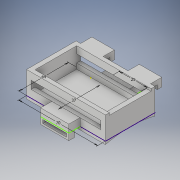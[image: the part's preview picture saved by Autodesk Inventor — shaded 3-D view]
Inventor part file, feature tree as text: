
AUTODESK INVENTOR PART (.ipt)
format: ipt  version: 2019 (Build 230136000, 136)  size: 488,448 bytes
history: native  units: mm
features: extrude x24, sketch x18
ambient origin geometry x8: Origin, YZ Plane, XZ Plane, XY Plane, X Axis, Y Axis, Z Axis, Center Point
bodies: Body1 (feature_tree)
feature tree (42):
  sketch  "Sketch1"  dims[d2=70.0mm d3=44.0mm]
  extrude  "Extrusion2"  Depth=44.0mm
  extrude  "Extrusion3"  Depth=2.0mm TaperAngle=0.0deg
  extrude  "Extrusion4"  Depth=25.0mm
  extrude  "Extrusion5"  Depth=2.0mm TaperAngle=0.0deg
  extrude  "Extrusion6"  Depth=20.0mm
  extrude  "Extrusion9"  Depth=20.0mm
  extrude  "Extrusion10"  Depth=5.0mm TaperAngle=0.0deg
  extrude  "Extrusion11"  Depth=10.0mm TaperAngle=0.0deg
  extrude  "Extrusion12"  Depth=90.0mm
  extrude  "Extrusion13"  Depth=2.0mm
  sketch  "Sketch6"  dims[d30=5.0mm d31=0.0mm d32=20.0mm]
  sketch  "Sketch7"  dims[d34=2.5mm d35=5.0mm d36=0.0mm]
  sketch  "Sketch8"  dims[d37=10.0mm d38=0.0mm d39=10.0mm d40=0.0mm]
  sketch  "Sketch9"  dims[d42=90.0mm d43=180.0mm]
  extrude  "Extrusion18"  Depth=2.0mm TaperAngle=0.0deg
  sketch  "Sketch21"  dims[d47=2.0mm d65=2.0mm d66=0.0mm]
  sketch  "Sketch25"  dims[d84=7.5mm d91=20.0mm]
  extrude  "Extrusion29"  Depth=20.0mm
  extrude  "Extrusion30"  Depth=20.0mm
  extrude  "Extrusion31"  Depth=6.0mm TaperAngle=0.0deg
  extrude  "Extrusion32"  Depth=21.0mm
  sketch  "Sketch30"  dims[d109=6.0mm d110=0.0mm d111=21.0mm]
  extrude  "Extrusion33"  Depth=6.0mm TaperAngle=0.0deg
  extrude  "Extrusion34"  Depth=6.0mm TaperAngle=0.0deg
  extrude  "Extrusion35"  Depth=6.75mm TaperAngle=0.0deg
  extrude  "Extrusion36"  Depth=6.75mm TaperAngle=0.0deg
  extrude  "Extrusion37"  Depth=6.75mm TaperAngle=0.0deg
  extrude  "Extrusion38"  Depth=6.75mm TaperAngle=0.0deg
  extrude  "Extrusion39"  Depth=10.0mm TaperAngle=0.0deg
  extrude  "Extrusion40"  Depth=10.0mm TaperAngle=0.0deg
  extrude  "Extrusion41"  Depth=20.0mm TaperAngle=0.0deg
  sketch  "Sketch34"  dims[d118=6.75mm d119=0.0mm d120=6.75mm d121=0.0mm d122=6.75mm d123=0.0mm d124=6.75mm d125=0.0mm d126=6.75mm d127=0.0mm d128=10.0mm d129=0.0mm d130=10.0mm d131=0.0mm d133=20.0mm d134=0.0mm d135=20.0mm d136=0.0mm d139=1.0mm d140=1.0mm d141=1.0mm d142=0.15mm d143=0.25mm d144=0.375mm d145=14.3117mm d146=0.75mm d147=20.594885mm d148=0.0625mm d149=0.75mm d150=0.375mm]
  sketch  "Sketch2"  dims[d6=20.0mm d7=0.0mm d8=2.0mm d9=0.0mm]
  sketch  "Sketch3"  dims[d10=45.0mm d11=0.0mm d16=25.0mm]
  sketch  "Sketch4"  dims[d20=2.0mm d21=0.0mm d22=2.0mm d23=0.0mm]
  sketch  "Sketch5"  dims[d28=20.0mm d29=2.5mm]
  sketch  "Sketch14"  dims[d44=70.0mm d45=0.0mm d46=2.0mm]
  sketch  "Sketch28"  dims[d97=37.0mm d98=20.0mm]
  sketch  "Sketch29"  dims[d99=7.5mm d107=6.0mm d108=0.0mm]
  sketch  "Sketch32"  dims[d112=3.0mm d113=6.0mm d114=0.0mm]
  sketch  "Sketch33"  dims[d115=21.0mm d116=6.0mm d117=0.0mm]
